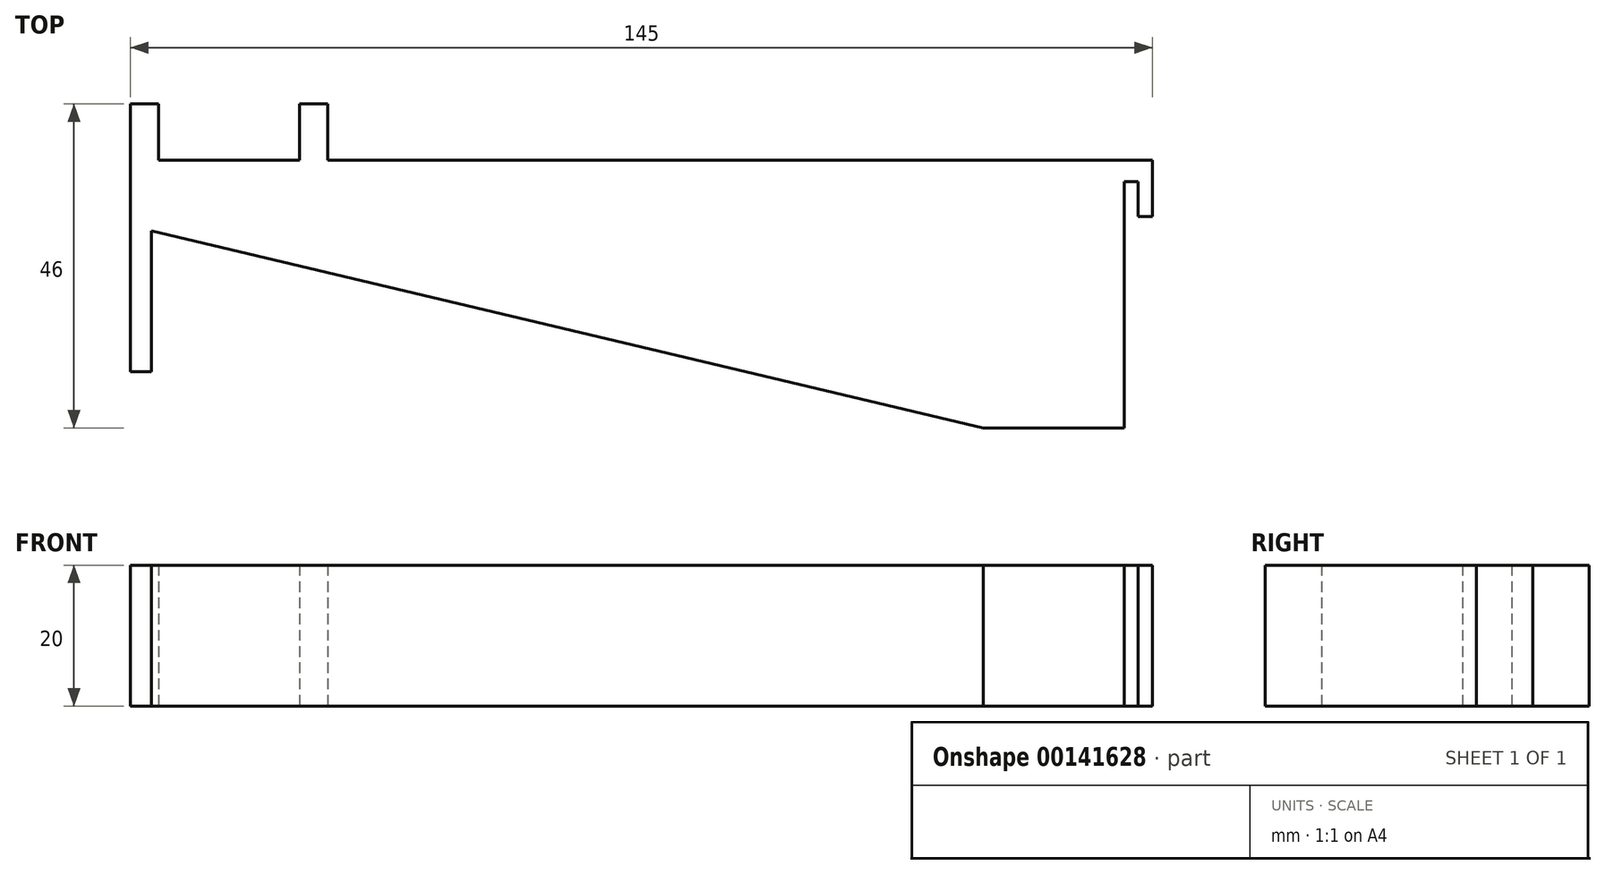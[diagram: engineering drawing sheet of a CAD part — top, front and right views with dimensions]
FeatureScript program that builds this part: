
annotation { "Feature Type Name" : "Feature", "Feature Type Description" : "" }
export const myFeature = defineFeature(function(context is Context, id is Id, definition is map)
    precondition{}
    {
        {
            var Q0;
            Q0=qCreatedBy(makeId("Top.planeOp"),FACE);
            var sketch = newSketch(context, id + "F0", { "sketchPlane" : qUnion([Q0])});
            skLineSegment(sketch, "E0", {"start": v(0, -35) * mm, "end": v(0, 0) * mm});
            skLineSegment(sketch, "E1", {"start": v(0, 0) * mm, "end": v(2, 0) * mm});
            skLineSegment(sketch, "E2", {"start": v(2, 0) * mm, "end": v(2, -5) * mm});
            skLineSegment(sketch, "E3", {"start": v(2, -5) * mm, "end": v(4, -5) * mm});
            skLineSegment(sketch, "E4", {"start": v(4, -5) * mm, "end": v(4, 3) * mm});
            skLineSegment(sketch, "E5", {"start": v(4, 3) * mm, "end": v(-141, 3) * mm});
            skLineSegment(sketch, "E6", {"start": v(-141, 3) * mm, "end": v(-141, 11) * mm});
            skLineSegment(sketch, "E7", {"start": v(-141, 11) * mm, "end": v(-137, 11) * mm});
            skLineSegment(sketch, "E8", {"start": v(-137, 11) * mm, "end": v(-137, 3) * mm});
            skLineSegment(sketch, "E9", {"start": v(-137, 3) * mm, "end": v(-117, 3) * mm});
            skLineSegment(sketch, "E10", {"start": v(-117, 3) * mm, "end": v(-117, 11) * mm});
            skLineSegment(sketch, "E11", {"start": v(-117, 11) * mm, "end": v(-113, 11) * mm});
            skLineSegment(sketch, "E12", {"start": v(-113, 11) * mm, "end": v(-113, 3) * mm});
            skLineSegment(sketch, "E13", {"start": v(-141, 3) * mm, "end": v(-141, -27) * mm});
            skLineSegment(sketch, "E14", {"start": v(-141, -27) * mm, "end": v(-138, -27) * mm});
            skLineSegment(sketch, "E15", {"start": v(-138, -27) * mm, "end": v(-138, -7) * mm});
            skLineSegment(sketch, "E16", {"start": v(0, -35) * mm, "end": v(-20, -35) * mm});
            skLineSegment(sketch, "E17", {"start": v(-20, -35) * mm, "end": v(-138, -7) * mm});
            skSolve(sketch);
        }
        {
            var Q0;
            Q0=makeQuery(id+"F0.imprint","IMPRINT",FACE,{"disambiguationData":[TD([[makeQuery(id+"F0.imprint","IMPRINT",EDGE,{"derivedFrom":sQuery(id+"F0.wireOp",EDGE,"E0")}),1.0]])]});
            var Q1;
            {var subQ0=sQuery(id+"F0.wireOp",EDGE,"E6");Q1=makeQuery(id+"F0.imprint","IMPRINT",FACE,{"disambiguationData":[TD([[makeQuery(id+"F0.imprint","IMPRINT",EDGE,{"derivedFrom":subQ0}),-1.0]])]});}
            var Q2;
            {var subQ0=sQuery(id+"F0.wireOp",EDGE,"E10");Q2=makeQuery(id+"F0.imprint","IMPRINT",FACE,{"disambiguationData":[TD([[makeQuery(id+"F0.imprint","IMPRINT",EDGE,{"derivedFrom":subQ0}),-1.0]])]});}
            extrude(context, id + "F1", {"entities" : qUnion([Q0, Q1, Q2]), "depth" : 20 * mm});
        }
    });
